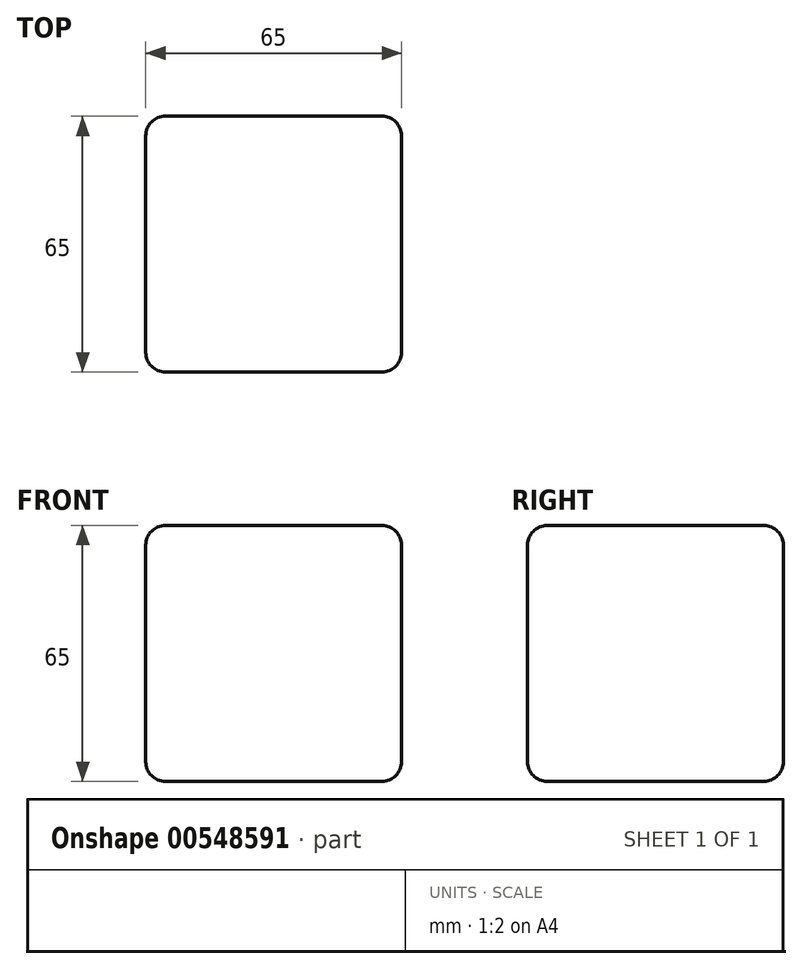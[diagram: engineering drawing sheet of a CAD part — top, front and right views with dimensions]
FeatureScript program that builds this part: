
annotation { "Feature Type Name" : "Feature", "Feature Type Description" : "" }
export const myFeature = defineFeature(function(context is Context, id is Id, definition is map)
    precondition{}
    {
        {
            var Q0;
            Q0=qCreatedBy(makeId("Front.planeOp"),FACE);
            var sketch = newSketch(context, id + "F0", { "sketchPlane" : qUnion([Q0])});
            skLineSegment(sketch, "E0.bottom", {"start": v(-32.5, 32.5) * mm, "end": v(32.5, 32.5) * mm});
            skLineSegment(sketch, "E0.top", {"start": v(-32.5, -32.5) * mm, "end": v(32.5, -32.5) * mm});
            skLineSegment(sketch, "E0.left", {"start": v(-32.5, 32.5) * mm, "end": v(-32.5, -32.5) * mm});
            skLineSegment(sketch, "E0.right", {"start": v(32.5, 32.5) * mm, "end": v(32.5, -32.5) * mm});
            skPoint(sketch, "E0.middle", {"position": v(0, 0) * mm});
            skSolve(sketch);
        }
        {
            var Q0;
            Q0=makeQuery(id+"F0.imprint","IMPRINT",FACE,{"disambiguationData":[TD([[makeQuery(id+"F0.imprint","IMPRINT",EDGE,{"derivedFrom":sQuery(id+"F0.wireOp",EDGE,"E0.bottom")}),-1.0]])]});
            extrude(context, id + "F1", {"entities" : qUnion([Q0]), "endBound" : BoundingType.SYMMETRIC, "depth" : 65 * mm, "offsetDistance" : 25 * mm});
        }
        {
            var Q0;
            Q0=makeQuery(id+"F1.opExtrude","CAP_EDGE",EDGE,{"disambiguationData":[OSD([sQuery(id+"F0.wireOp",EDGE,"E0.bottom")])],"isStart":false});
            var Q1;
            Q1=makeQuery(id+"F1.opExtrude","CAP_EDGE",EDGE,{"disambiguationData":[OSD([sQuery(id+"F0.wireOp",EDGE,"E0.right")])],"isStart":false});
            var Q2;
            Q2=makeQuery(id+"F1.opExtrude","SWEPT_EDGE",EDGE,{"disambiguationData":[OSD([sQuery(id+"F0.wireOp",EDGE,"E0.bottom"),sQuery(id+"F0.wireOp",EDGE,"E0.right")])]});
            var Q3;
            Q3=makeQuery(id+"F1.opExtrude","SWEPT_EDGE",EDGE,{"disambiguationData":[OSD([sQuery(id+"F0.wireOp",EDGE,"E0.top"),sQuery(id+"F0.wireOp",EDGE,"E0.right")])]});
            var Q4;
            Q4=makeQuery(id+"F1.opExtrude","CAP_EDGE",EDGE,{"disambiguationData":[OSD([sQuery(id+"F0.wireOp",EDGE,"E0.top")])],"isStart":false});
            var Q5;
            Q5=makeQuery(id+"F1.opExtrude","CAP_EDGE",EDGE,{"disambiguationData":[OSD([sQuery(id+"F0.wireOp",EDGE,"E0.left")])],"isStart":false});
            var Q6;
            Q6=makeQuery(id+"F1.opExtrude","SWEPT_EDGE",EDGE,{"disambiguationData":[OSD([sQuery(id+"F0.wireOp",EDGE,"E0.top"),sQuery(id+"F0.wireOp",EDGE,"E0.left")])]});
            var Q7;
            Q7=makeQuery(id+"F1.opExtrude","SWEPT_EDGE",EDGE,{"disambiguationData":[OSD([sQuery(id+"F0.wireOp",EDGE,"E0.bottom"),sQuery(id+"F0.wireOp",EDGE,"E0.left")])]});
            var Q8;
            Q8=makeQuery(id+"F1.opExtrude","CAP_EDGE",EDGE,{"disambiguationData":[OSD([sQuery(id+"F0.wireOp",EDGE,"E0.left")])],"isStart":true});
            var Q9;
            Q9=makeQuery(id+"F1.opExtrude","CAP_EDGE",EDGE,{"disambiguationData":[OSD([sQuery(id+"F0.wireOp",EDGE,"E0.top")])],"isStart":true});
            var Q10;
            Q10=makeQuery(id+"F1.opExtrude","CAP_EDGE",EDGE,{"disambiguationData":[OSD([sQuery(id+"F0.wireOp",EDGE,"E0.right")])],"isStart":true});
            var Q11;
            Q11=makeQuery(id+"F1.opExtrude","CAP_EDGE",EDGE,{"disambiguationData":[OSD([sQuery(id+"F0.wireOp",EDGE,"E0.bottom")])],"isStart":true});
            fillet(context, id + "F2", {"entities" : qUnion([Q0, Q1, Q2, Q3, Q4, Q5, Q6, Q7, Q8, Q9, Q10, Q11]), "radius" : 5 * mm, "tangentPropagation" : true, "allowEdgeOverflow" : false});
        }
    });
